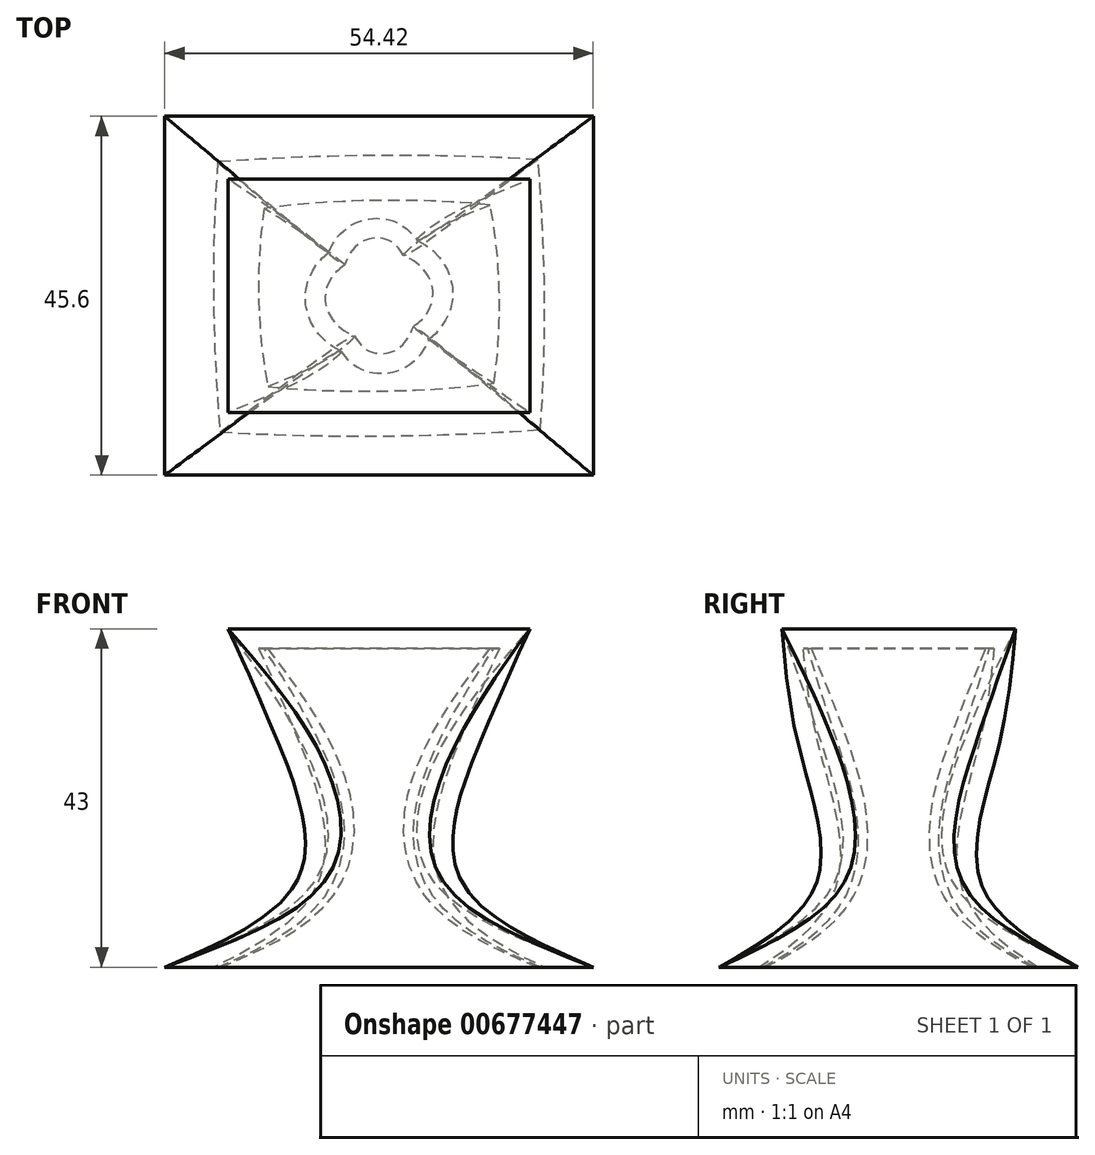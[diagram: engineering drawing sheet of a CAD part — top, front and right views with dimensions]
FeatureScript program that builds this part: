
annotation { "Feature Type Name" : "Feature", "Feature Type Description" : "" }
export const myFeature = defineFeature(function(context is Context, id is Id, definition is map)
    precondition{}
    {
        {
            var Q0;
            Q0=qCreatedBy(makeId("Top.planeOp"),FACE);
            var sketch = newSketch(context, id + "F0", { "sketchPlane" : qUnion([Q0])});
            skLineSegment(sketch, "E0.bottom", {"start": v(27.21, -22.8) * mm, "end": v(-27.21, -22.8) * mm});
            skLineSegment(sketch, "E0.top", {"start": v(27.21, 22.8) * mm, "end": v(-27.21, 22.8) * mm});
            skLineSegment(sketch, "E0.left", {"start": v(27.21, -22.8) * mm, "end": v(27.21, 22.8) * mm});
            skLineSegment(sketch, "E0.right", {"start": v(-27.21, -22.8) * mm, "end": v(-27.21, 22.8) * mm});
            skPoint(sketch, "E0.middle", {"position": v(0, 0) * mm});
            skSolve(sketch);
        }
        {
            var Q0;
            Q0=qCreatedBy(makeId("Top.planeOp"),FACE);
            cPlane(context, id + "F1", {"entities" : qUnion([Q0]), "cplaneType" : CPlaneType.OFFSET, "offset" : 43 * mm, "width" : 150 * mm, "height" : 150 * mm});
        }
        {
            var Q0;
            Q0=qCreatedBy(id+"F1.planeOp",FACE);
            var sketch = newSketch(context, id + "F2", { "sketchPlane" : qUnion([Q0])});
            skLineSegment(sketch, "E1.bottom", {"start": v(19.18, -14.84) * mm, "end": v(-19.18, -14.84) * mm});
            skLineSegment(sketch, "E1.top", {"start": v(19.18, 14.84) * mm, "end": v(-19.18, 14.84) * mm});
            skLineSegment(sketch, "E1.left", {"start": v(19.18, -14.84) * mm, "end": v(19.18, 14.84) * mm});
            skLineSegment(sketch, "E1.right", {"start": v(-19.18, -14.84) * mm, "end": v(-19.18, 14.84) * mm});
            skPoint(sketch, "E1.middle", {"position": v(0, 0) * mm});
            skSolve(sketch);
        }
        {
            var Q0;
            Q0=qCreatedBy(makeId("Top.planeOp"),FACE);
            cPlane(context, id + "F3", {"entities" : qUnion([Q0]), "cplaneType" : CPlaneType.OFFSET, "offset" : 11.4 * mm, "width" : 150 * mm, "height" : 150 * mm});
        }
        {
            var Q0;
            Q0=qCreatedBy(makeId("Top.planeOp"),FACE);
            cPlane(context, id + "F4", {"entities" : qUnion([Q0]), "cplaneType" : CPlaneType.OFFSET, "offset" : 28.5 * mm, "width" : 150 * mm, "height" : 150 * mm});
        }
        {
            var Q0;
            Q0=qCreatedBy(id+"F3.planeOp",FACE);
            var sketch = newSketch(context, id + "F5", { "sketchPlane" : qUnion([Q0])});
            skCircle(sketch, "E2", {"center": v(0, 0) * mm, "radius": 10.21 * mm});
            skSolve(sketch);
        }
        {
            var Q0;
            Q0=qCreatedBy(id+"F4.planeOp",FACE);
            var sketch = newSketch(context, id + "F6", { "sketchPlane" : qUnion([Q0])});
            skCircle(sketch, "E3", {"center": v(0, 0) * mm, "radius": 12.8 * mm});
            skSolve(sketch);
        }
        {
            var Q0;
            Q0=makeQuery(id+"F0.imprint","IMPRINT",FACE,{"disambiguationData":[TD([[makeQuery(id+"F0.imprint","IMPRINT",EDGE,{"derivedFrom":sQuery(id+"F0.wireOp",EDGE,"E0.bottom")}),-1.0]])]});
            var Q1;
            Q1=makeQuery(id+"F5.imprint","IMPRINT",FACE,{"disambiguationData":[TD([[makeQuery(id+"F5.imprint","IMPRINT",EDGE,{"derivedFrom":sQuery(id+"F5.wireOp",EDGE,"E2")}),1.0]])]});
            var Q2;
            Q2=makeQuery(id+"F6.imprint","IMPRINT",FACE,{"disambiguationData":[TD([[makeQuery(id+"F6.imprint","IMPRINT",EDGE,{"derivedFrom":sQuery(id+"F6.wireOp",EDGE,"E3")}),1.0]])]});
            var Q3;
            Q3=makeQuery(id+"F2.imprint","IMPRINT",FACE,{"disambiguationData":[TD([[makeQuery(id+"F2.imprint","IMPRINT",EDGE,{"derivedFrom":sQuery(id+"F2.wireOp",EDGE,"E1.bottom")}),-1.0]])]});
            loft(context, id + "F7", {"sheetProfilesArray" : [{ "sheetProfileEntities" : qUnion([Q0]) }, { "sheetProfileEntities" : qUnion([Q1]) }, { "sheetProfileEntities" : qUnion([Q2]) }, { "sheetProfileEntities" : qUnion([Q3]) }]});
        }
        {
            var Q0;
            Q0=makeQuery(id+"F7.opLoft","CAP_FACE",FACE,{"disambiguationData":[OSD([makeQuery(id+"F0.imprint","IMPRINT",FACE,{"disambiguationData":[TD([[makeQuery(id+"F0.imprint","IMPRINT",EDGE,{"derivedFrom":sQuery(id+"F0.wireOp",EDGE,"E0.bottom")}),-1.0]])]})])],"isStart":true});
            shell(context, id + "F8", {"entities" : qUnion([Q0]), "thickness" : 2.5 * mm});
        }
    });
